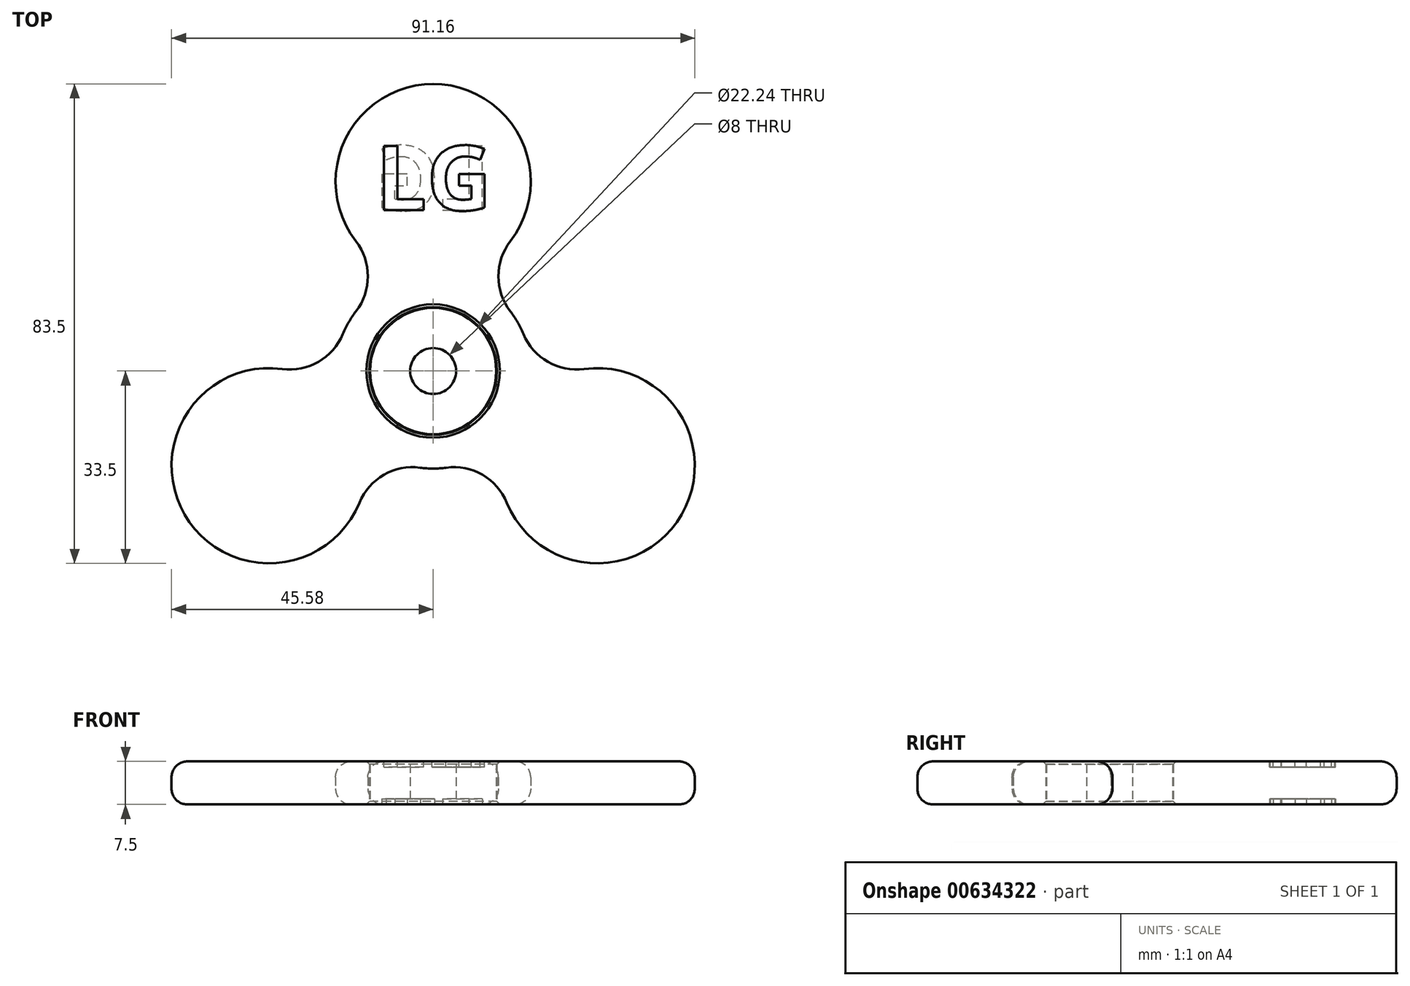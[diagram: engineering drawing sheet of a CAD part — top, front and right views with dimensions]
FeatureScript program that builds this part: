
annotation { "Feature Type Name" : "Feature", "Feature Type Description" : "" }
export const myFeature = defineFeature(function(context is Context, id is Id, definition is map)
    precondition{}
    {
        {
            var Q0;
            Q0=qCreatedBy(makeId("Top.planeOp"),FACE);
            var sketch = newSketch(context, id + "F0", { "sketchPlane" : qUnion([Q0])});
            skCircle(sketch, "E0", {"center": v(0, 0) * mm, "radius": 4 * mm});
            skCircle(sketch, "E1", {"center": v(0, 0) * mm, "radius": 11 * mm});
            skSolve(sketch);
        }
        {
            var Q0;
            Q0=makeQuery(id+"F0.imprint","IMPRINT",FACE,{"disambiguationData":[TD([[makeQuery(id+"F0.imprint","IMPRINT",EDGE,{"derivedFrom":sQuery(id+"F0.wireOp",EDGE,"E0")}),-1.0]])]});
            extrude(context, id + "F1", {"entities" : qUnion([Q0]), "depth" : 7 * mm, "offsetDistance" : 25 * mm});
        }
        {
            var Q0;
            Q0=qCreatedBy(makeId("Top.planeOp"),FACE);
            var sketch = newSketch(context, id + "F2", { "sketchPlane" : qUnion([Q0])});
            skArc(sketch, "E2.0", {"start": v(-2.27, -16.85) * mm, "mid": v(0, -17) * mm, "end": v(2.27, -16.85) * mm});
            skCircle(sketch, "E3.0", {"center": v(0, 0) * mm, "radius": 11.12 * mm});
            skArc(sketch, "E4", {"start": v(13.46, 22.61) * mm, "mid": v(0, 50) * mm, "end": v(-13.46, 22.61) * mm});
            skArc(sketch, "E5.1.0", {"start": v(-26.3, 0.35) * mm, "mid": v(-43.3, -25) * mm, "end": v(-12.85, -22.96) * mm});
            skArc(sketch, "E5.2.0", {"start": v(12.85, -22.96) * mm, "mid": v(43.3, -25) * mm, "end": v(26.3, 0.35) * mm});
            skArc(sketch, "E6.trimOffspring", {"start": v(-13.46, 10.39) * mm, "mid": v(-14.72, 8.5) * mm, "end": v(-15.73, 6.46) * mm});
            skArc(sketch, "E7.trimOffspring", {"start": v(15.73, 6.46) * mm, "mid": v(14.72, 8.5) * mm, "end": v(13.46, 10.39) * mm});
            skPoint(sketch, "E8.visualSharp", {"position": v(-4.1, 16.5) * mm});
            skArc(sketch, "E8.filletArc", {"start": v(-13.46, 10.39) * mm, "mid": v(-11.37, 16.5) * mm, "end": v(-13.46, 22.61) * mm});
            skPoint(sketch, "E9.visualSharp", {"position": v(4.1, 16.5) * mm});
            skArc(sketch, "E9.filletArc", {"start": v(13.46, 22.61) * mm, "mid": v(11.37, 16.5) * mm, "end": v(13.46, 10.39) * mm});
            skPoint(sketch, "E10.visualSharp", {"position": v(16.34, -4.7) * mm});
            skArc(sketch, "E10.filletArc", {"start": v(15.73, 6.46) * mm, "mid": v(19.98, 1.6) * mm, "end": v(26.3, 0.35) * mm});
            skPoint(sketch, "E11.visualSharp", {"position": v(12.24, -11.8) * mm});
            skArc(sketch, "E11.filletArc", {"start": v(12.85, -22.96) * mm, "mid": v(8.6, -18.1) * mm, "end": v(2.27, -16.85) * mm});
            skPoint(sketch, "E12.visualSharp", {"position": v(-12.24, -11.8) * mm});
            skArc(sketch, "E12.filletArc", {"start": v(-2.27, -16.85) * mm, "mid": v(-8.6, -18.1) * mm, "end": v(-12.85, -22.96) * mm});
            skPoint(sketch, "E13.visualSharp", {"position": v(-16.34, -4.7) * mm});
            skArc(sketch, "E13.filletArc", {"start": v(-26.3, 0.35) * mm, "mid": v(-19.98, 1.6) * mm, "end": v(-15.73, 6.46) * mm});
            skSolve(sketch);
        }
        {
            var Q0;
            Q0=makeQuery(id+"F2.imprint","IMPRINT",FACE,{"disambiguationData":[TD([[makeQuery(id+"F2.imprint","IMPRINT",EDGE,{"derivedFrom":sQuery(id+"F2.wireOp",EDGE,"E2.0")}),1.0]])]});
            extrude(context, id + "F3", {"entities" : qUnion([Q0]), "depth" : 7.5 * mm, "offsetDistance" : 25 * mm});
        }
        {
            var Q0;
            Q0=makeQuery(id+"F3.opExtrude","CAP_EDGE",EDGE,{"disambiguationData":[OSD([sQuery(id+"F2.wireOp",EDGE,"E12.filletArc")])],"isStart":false});
            var Q1;
            Q1=makeQuery(id+"F3.opExtrude","CAP_EDGE",EDGE,{"disambiguationData":[OSD([sQuery(id+"F2.wireOp",EDGE,"E4")])],"isStart":true});
            fillet(context, id + "F4", {"entities" : qUnion([Q0, Q1]), "radius" : 2.75 * mm, "tangentPropagation" : true, "allowEdgeOverflow" : false});
        }
        {
            var Q0;
            Q0=makeQuery(id+"F3.opExtrude","CAP_FACE",FACE,{"disambiguationData":[OSD([sQuery(id+"F2.wireOp",EDGE,"E2.0"),sQuery(id+"F2.wireOp",EDGE,"E3.0"),sQuery(id+"F2.wireOp",EDGE,"E4"),sQuery(id+"F2.wireOp",EDGE,"E5.1.0"),sQuery(id+"F2.wireOp",EDGE,"E5.2.0"),sQuery(id+"F2.wireOp",EDGE,"E6.trimOffspring"),sQuery(id+"F2.wireOp",EDGE,"E7.trimOffspring"),sQuery(id+"F2.wireOp",EDGE,"E8.filletArc"),sQuery(id+"F2.wireOp",EDGE,"E9.filletArc"),sQuery(id+"F2.wireOp",EDGE,"E10.filletArc"),sQuery(id+"F2.wireOp",EDGE,"E11.filletArc"),sQuery(id+"F2.wireOp",EDGE,"E12.filletArc"),sQuery(id+"F2.wireOp",EDGE,"E13.filletArc")])],"isStart":false});
            var sketch = newSketch(context, id + "F5", { "sketchPlane" : qUnion([Q0])});
            skText(sketch, "E14", { "text": "LG\n", "fontName": "OpenSans-Bold.ttf"});
            const initialGuessF5  = {"E14": [-0.01, 0.028, 1, 0, 0.0113]};
            skSetInitialGuess(sketch, initialGuessF5);
            skSolve(sketch);
        }
        {
            var Q0;
            Q0=qSketchRegion(id+"F5",true);
            extrude(context, id + "F6", {"entities" : qUnion([Q0]), "operationType" : NewBodyOperationType.REMOVE, "oppositeDirection" : true, "depth" : 1 * mm, "offsetDistance" : 25 * mm});
        }
        {
            var Q0;
            Q0=makeQuery(id+"F3.opExtrude","CAP_FACE",FACE,{"disambiguationData":[OSD([sQuery(id+"F2.wireOp",EDGE,"E2.0"),sQuery(id+"F2.wireOp",EDGE,"E3.0"),sQuery(id+"F2.wireOp",EDGE,"E4"),sQuery(id+"F2.wireOp",EDGE,"E5.1.0"),sQuery(id+"F2.wireOp",EDGE,"E5.2.0"),sQuery(id+"F2.wireOp",EDGE,"E6.trimOffspring"),sQuery(id+"F2.wireOp",EDGE,"E7.trimOffspring"),sQuery(id+"F2.wireOp",EDGE,"E8.filletArc"),sQuery(id+"F2.wireOp",EDGE,"E9.filletArc"),sQuery(id+"F2.wireOp",EDGE,"E10.filletArc"),sQuery(id+"F2.wireOp",EDGE,"E11.filletArc"),sQuery(id+"F2.wireOp",EDGE,"E12.filletArc"),sQuery(id+"F2.wireOp",EDGE,"E13.filletArc")])],"isStart":true});
            var sketch = newSketch(context, id + "F7", { "sketchPlane" : qUnion([Q0])});
            skText(sketch, "E15", { "text": "LG", "fontName": "OpenSans-Bold.ttf"});
            const initialGuessF7  = {"E15": [0.01, -0.028, -1, 0, 0.0113]};
            skSetInitialGuess(sketch, initialGuessF7);
            skSolve(sketch);
        }
        {
            var Q0;
            Q0=qSketchRegion(id+"F7",true);
            extrude(context, id + "F8", {"entities" : qUnion([Q0]), "operationType" : NewBodyOperationType.REMOVE, "oppositeDirection" : true, "depth" : 1 * mm, "offsetDistance" : 25 * mm});
        }
        {
            var Q0;
            Q0=makeQuery(id+"F3.opExtrude","CAP_EDGE",EDGE,{"disambiguationData":[OSD([sQuery(id+"F2.wireOp",EDGE,"E3.0")])],"isStart":false});
            var Q1;
            Q1=makeQuery(id+"F3.opExtrude","CAP_EDGE",EDGE,{"disambiguationData":[OSD([sQuery(id+"F2.wireOp",EDGE,"E3.0")])],"isStart":true});
            chamfer(context, id + "F9", {"entities" : qUnion([Q0, Q1]), "width" : .5 * mm, "tangentPropagation" : true});
        }
    });
